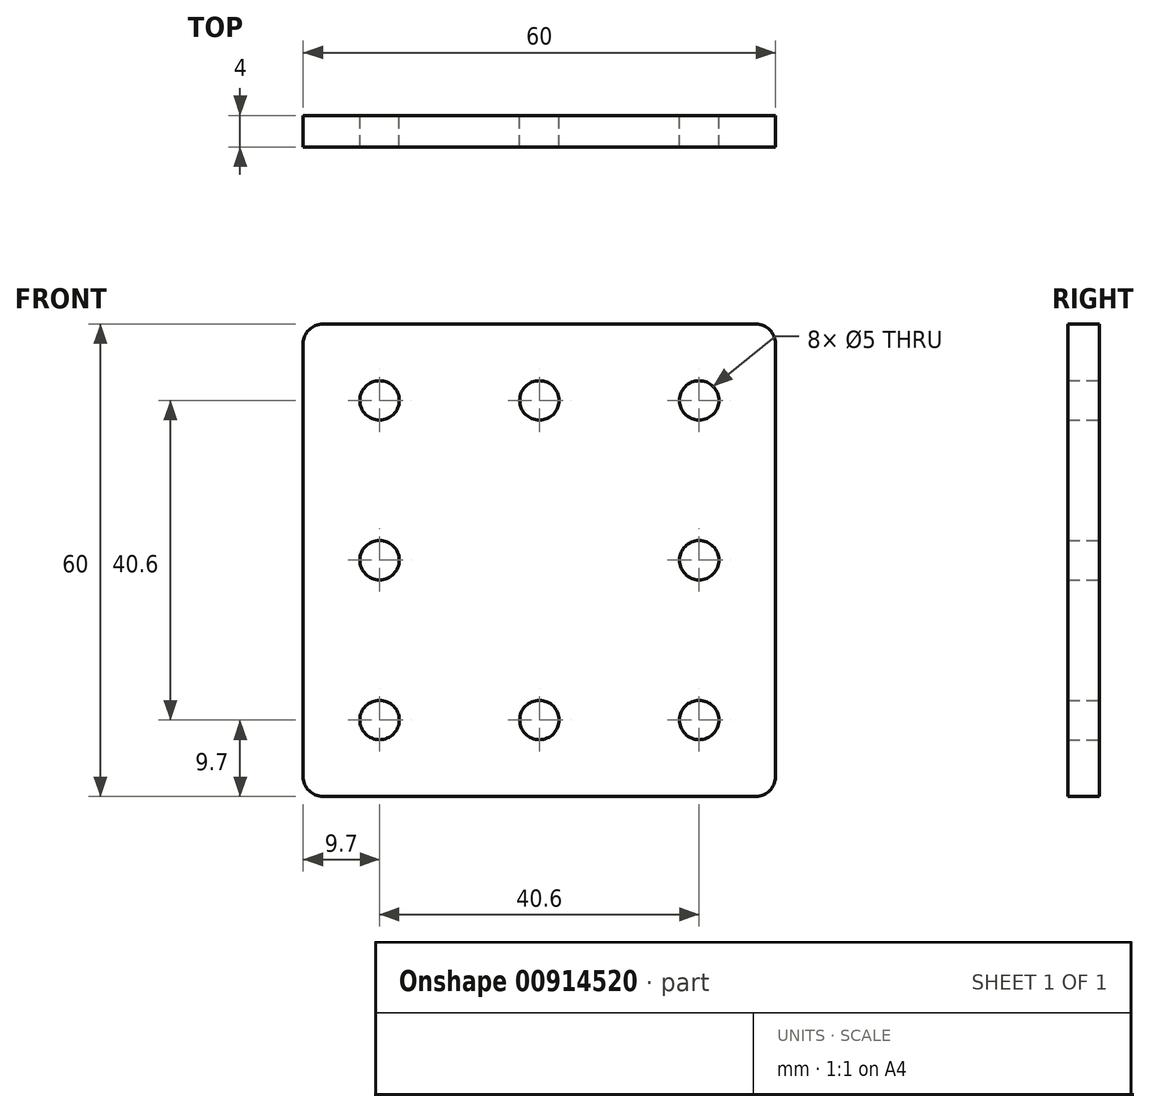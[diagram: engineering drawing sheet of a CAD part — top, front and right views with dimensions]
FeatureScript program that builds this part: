
annotation { "Feature Type Name" : "Feature", "Feature Type Description" : "" }
export const myFeature = defineFeature(function(context is Context, id is Id, definition is map)
    precondition{}
    {
        {
            var Q0;
            Q0=qCreatedBy(makeId("Front.planeOp"),FACE);
            var sketch = newSketch(context, id + "F0", { "sketchPlane" : qUnion([Q0])});
            skLineSegment(sketch, "E0.bottom", {"start": v(30, 30) * mm, "end": v(-30, 30) * mm});
            skLineSegment(sketch, "E0.top", {"start": v(30, -30) * mm, "end": v(-30, -30) * mm});
            skLineSegment(sketch, "E0.left", {"start": v(30, 30) * mm, "end": v(30, -30) * mm});
            skLineSegment(sketch, "E0.right", {"start": v(-30, 30) * mm, "end": v(-30, -30) * mm});
            skPoint(sketch, "E0.middle", {"position": v(0, 0) * mm});
            skLineSegment(sketch, "E1", {"start": v(20.3, 30) * mm, "end": v(20.3, -30) * mm, "construction": true});
            skLineSegment(sketch, "E2", {"start": v(30, 20.3) * mm, "end": v(-30, 20.3) * mm, "construction": true});
            skLineSegment(sketch, "E3.MirrorCS", {"start": v(-20.3, 30) * mm, "end": v(-20.3, -30) * mm, "construction": true});
            skLineSegment(sketch, "E4.MirrorCS", {"start": v(30, -20.3) * mm, "end": v(-30, -20.3) * mm, "construction": true});
            skPoint(sketch, "E5", {"position": v(-20.3, 20.3) * mm});
            skPoint(sketch, "E6", {"position": v(20.3, 20.3) * mm});
            skPoint(sketch, "E7", {"position": v(20.3, -20.3) * mm});
            skPoint(sketch, "E8", {"position": v(-20.3, -20.3) * mm});
            skPoint(sketch, "E9", {"position": v(0, 20.3) * mm});
            skPoint(sketch, "E10", {"position": v(0, -20.3) * mm});
            skPoint(sketch, "E11", {"position": v(-20.3, 0) * mm});
            skPoint(sketch, "E12", {"position": v(20.3, 0) * mm});
            skSolve(sketch);
        }
        {
            var Q0;
            Q0=qSketchRegion(id+"F0",true);
            extrude(context, id + "F1", {"entities" : qUnion([Q0]), "depth" : 4 * mm, "offsetDistance" : 25 * mm});
        }
        {
            var Q0;
            Q0=sQuery(id+"F0.wireOp",VERTEX,"E8");
            var Q1;
            Q1=sQuery(id+"F0.wireOp",VERTEX,"E7");
            var Q2;
            Q2=sQuery(id+"F0.wireOp",VERTEX,"E6");
            var Q3;
            Q3=sQuery(id+"F0.wireOp",VERTEX,"E5");
            var Q4;
            Q4=sQuery(id+"F0.wireOp",VERTEX,"E9");
            var Q5;
            Q5=sQuery(id+"F0.wireOp",VERTEX,"E12");
            var Q6;
            Q6=sQuery(id+"F0.wireOp",VERTEX,"E10");
            var Q7;
            Q7=sQuery(id+"F0.wireOp",VERTEX,"E11");
            var Q8;
            Q8=makeQuery(id+"F1.opExtrude","SWEPT_BODY",BODY,{"disambiguationData":[OSD([sQuery(id+"F0.wireOp",EDGE,"E0.bottom"),sQuery(id+"F0.wireOp",EDGE,"E0.top"),sQuery(id+"F0.wireOp",EDGE,"E0.left"),sQuery(id+"F0.wireOp",EDGE,"E0.right")])]});
            hole(context, id + "F2", {"style" : HoleStyle.SIMPLE, "endStyle" : HoleEndStyle.THROUGH, "oppositeDirection" : true, "holeDiameter" : 5 * mm, "majorDiameter" : 5 * mm, "isTappedThrough" : true, "tappedDepth" : 12 * mm, "tapClearance" : 3, "locations" : qUnion([Q0, Q1, Q2, Q3, Q4, Q5, Q6, Q7]), "scope" : qUnion([Q8])});
        }
        {
            var Q0;
            Q0=makeQuery(id+"F1.opExtrude","SWEPT_EDGE",EDGE,{"disambiguationData":[OSD([sQuery(id+"F0.wireOp",EDGE,"E0.bottom"),sQuery(id+"F0.wireOp",EDGE,"E0.left")])]});
            var Q1;
            Q1=makeQuery(id+"F1.opExtrude","SWEPT_EDGE",EDGE,{"disambiguationData":[OSD([sQuery(id+"F0.wireOp",EDGE,"E0.top"),sQuery(id+"F0.wireOp",EDGE,"E0.left")])]});
            var Q2;
            Q2=makeQuery(id+"F1.opExtrude","SWEPT_EDGE",EDGE,{"disambiguationData":[OSD([sQuery(id+"F0.wireOp",EDGE,"E0.top"),sQuery(id+"F0.wireOp",EDGE,"E0.right")])]});
            var Q3;
            Q3=makeQuery(id+"F1.opExtrude","SWEPT_EDGE",EDGE,{"disambiguationData":[OSD([sQuery(id+"F0.wireOp",EDGE,"E0.bottom"),sQuery(id+"F0.wireOp",EDGE,"E0.right")])]});
            fillet(context, id + "F3", {"entities" : qUnion([Q0, Q1, Q2, Q3]), "radius" : 2.5 * mm, "tangentPropagation" : true, "allowEdgeOverflow" : false});
        }
    });
